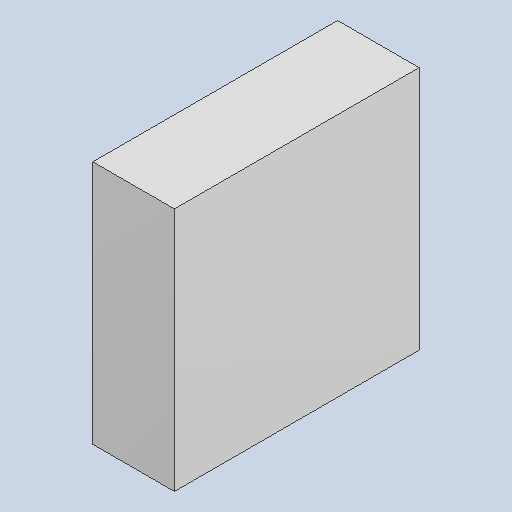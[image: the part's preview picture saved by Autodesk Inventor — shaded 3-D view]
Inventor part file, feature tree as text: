
AUTODESK INVENTOR PART (.ipt)
format: ipt  version: 2023.4 (Build 274418000, 418)  size: 81,408 bytes
history: native  units: mm
features: extrude x1
ambient origin geometry x8: Origin, YZ Plane, XZ Plane, XY Plane, X Axis, Y Axis, Z Axis, Center Point
bodies: Solid1 (feature_tree)
feature tree (1):
  extrude  "Extruded_38"  [1 undecoded]
note: 1 required parameter value undecoded (feature->parameter linkage not recoverable at this tier; creation-order binding heuristic only, values carry confidence <= 0.55)
